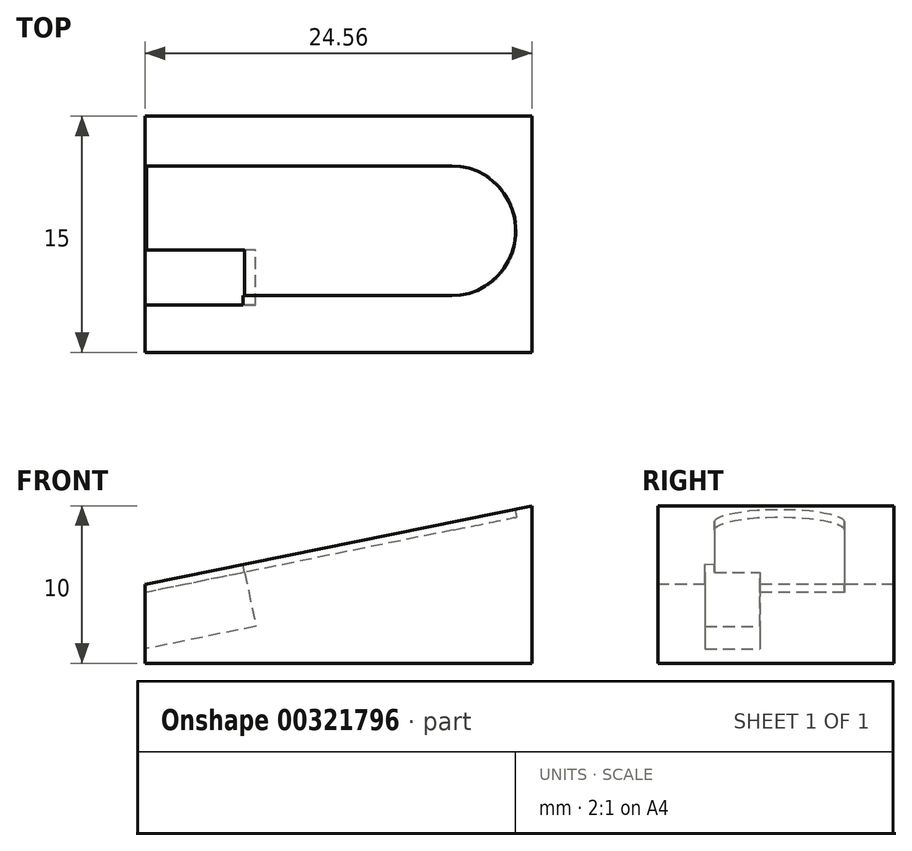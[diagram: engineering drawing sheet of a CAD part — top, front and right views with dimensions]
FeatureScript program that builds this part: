
annotation { "Feature Type Name" : "Feature", "Feature Type Description" : "" }
export const myFeature = defineFeature(function(context is Context, id is Id, definition is map)
    precondition{}
    {
        {
            var Q0;
            Q0=qCreatedBy(makeId("Front.planeOp"),FACE);
            var sketch = newSketch(context, id + "F0", { "sketchPlane" : qUnion([Q0])});
            skLineSegment(sketch, "E0.bottom", {"start": v(0, 24.14) * mm, "end": v(-24.56, 24.14) * mm});
            skLineSegment(sketch, "E0.top", {"start": v(0, 14.14) * mm, "end": v(-24.56, 14.14) * mm});
            skLineSegment(sketch, "E0.left", {"start": v(0, 24.14) * mm, "end": v(0, 14.14) * mm});
            skLineSegment(sketch, "E0.right", {"start": v(-24.56, 24.14) * mm, "end": v(-24.56, 14.14) * mm});
            skSolve(sketch);
        }
        {
            var Q0;
            Q0=makeQuery(id+"F0.imprint","IMPRINT",FACE,{"disambiguationData":[TD([[makeQuery(id+"F0.imprint","IMPRINT",EDGE,{"derivedFrom":sQuery(id+"F0.wireOp",EDGE,"E0.bottom")}),1.0]])]});
            extrude(context, id + "F1", {"entities" : qUnion([Q0]), "depth" : 15 * mm});
        }
        {
            var Q0;
            Q0=makeQuery(id+"F1.opExtrude","SWEPT_FACE",FACE,{"disambiguationData":[OSD([sQuery(id+"F0.wireOp",EDGE,"E0.left")])]});
            var sketch = newSketch(context, id + "F2", { "sketchPlane" : qUnion([Q0])});
            skLineSegment(sketch, "E1.bottom", {"start": v(-15, 24.14) * mm, "end": v(0, 24.14) * mm});
            skLineSegment(sketch, "E1.top", {"start": v(-15, 14.14) * mm, "end": v(0, 14.14) * mm});
            skLineSegment(sketch, "E1.left", {"start": v(-15, 24.14) * mm, "end": v(-15, 14.14) * mm});
            skLineSegment(sketch, "E1.right", {"start": v(0, 24.14) * mm, "end": v(0, 14.14) * mm});
            skSolve(sketch);
        }
        {
            var Q0;
            Q0=makeQuery(id+"F1.opExtrude","SWEPT_FACE",FACE,{"disambiguationData":[OSD([sQuery(id+"F0.wireOp",EDGE,"E0.right")])]});
            var sketch = newSketch(context, id + "F3", { "sketchPlane" : qUnion([Q0])});
            skLineSegment(sketch, "E2.bottom", {"start": v(0, 19.14) * mm, "end": v(15, 19.14) * mm});
            skLineSegment(sketch, "E2.top", {"start": v(0, 14.14) * mm, "end": v(15, 14.14) * mm});
            skLineSegment(sketch, "E2.left", {"start": v(0, 19.14) * mm, "end": v(0, 14.14) * mm});
            skLineSegment(sketch, "E2.right", {"start": v(15, 19.14) * mm, "end": v(15, 14.14) * mm});
            skSolve(sketch);
        }
        {
            var Q1;
            Q1 = qSketchRegion(id + "F2", true);
            var Q2;
            Q2=makeQuery(id+"F3.imprint","IMPRINT",FACE,{"disambiguationData":[TD([[makeQuery(id+"F3.imprint","IMPRINT",EDGE,{"derivedFrom":sQuery(id+"F3.wireOp",EDGE,"E2.bottom")}),-1.0]])]});
            loft(context, id + "F4", {"sheetProfilesArray" : [{ "sheetProfileEntities" : qUnion([Q1]) }, { "sheetProfileEntities" : qUnion([Q2]) }]});
        }
        {
            var Q0;
            Q0=makeQuery(id+"F1.opExtrude","SWEPT_BODY",BODY,{"disambiguationData":[OSD([sQuery(id+"F0.wireOp",EDGE,"E0.bottom"),sQuery(id+"F0.wireOp",EDGE,"E0.top"),sQuery(id+"F0.wireOp",EDGE,"E0.left"),sQuery(id+"F0.wireOp",EDGE,"E0.right")])]});
            deleteBodies(context, id + "F5", {"entities" : qUnion([Q0])});
        }
        {
            var Q0;
            Q0=makeQuery(id+"F4.opLoft","SWEPT_FACE",FACE,{"disambiguationData":[OSD([sQuery(id+"F0.wireOp",EDGE,"E0.right"),sQuery(id+"F2.wireOp",EDGE,"E1.bottom"),sQuery(id+"F2.wireOp",EDGE,"E1.left"),sQuery(id+"F2.wireOp",EDGE,"E1.right"),sQuery(id+"F3.wireOp",EDGE,"E2.bottom"),sQuery(id+"F3.wireOp",EDGE,"E2.left"),sQuery(id+"F3.wireOp",EDGE,"E2.right")])]});
            var sketch = newSketch(context, id + "F6", { "sketchPlane" : qUnion([Q0])});
            skArc(sketch, "E3", {"start": v(-0.36, -11.4) * mm, "mid": v(3.76, -7.28) * mm, "end": v(-0.36, -3.15) * mm});
            skLineSegment(sketch, "E4", {"start": v(-0.36, -3.15) * mm, "end": v(-20.25, -3.15) * mm});
            skLineSegment(sketch, "E5", {"start": v(-0.36, -11.4) * mm, "end": v(-13.9, -11.4) * mm});
            skLineSegment(sketch, "E6", {"start": v(-20.25, -12) * mm, "end": v(-13.9, -12) * mm});
            skLineSegment(sketch, "E7", {"start": v(-13.9, -11.4) * mm, "end": v(-13.9, -12) * mm});
            skSolve(sketch);
        }
        {
            var Q0;
            Q0=makeQuery(id+"F6.imprint","IMPRINT",FACE,{"disambiguationData":[TD([[makeQuery(id+"F6.imprint","IMPRINT",EDGE,{"derivedFrom":sQuery(id+"F6.wireOp",EDGE,"E3")}),1.0]])]});
            extrude(context, id + "F7", {"entities" : qUnion([Q0]), "operationType" : NewBodyOperationType.REMOVE, "oppositeDirection" : true, "depth" : 0.5 * mm});
        }
        {
            var Q0;
            Q0=makeQuery(id+"F4.opLoft","SWEPT_FACE",FACE,{"disambiguationData":[OSD([sQuery(id+"F0.wireOp",EDGE,"E0.right"),sQuery(id+"F2.wireOp",EDGE,"E1.bottom"),sQuery(id+"F2.wireOp",EDGE,"E1.left"),sQuery(id+"F2.wireOp",EDGE,"E1.right"),sQuery(id+"F3.wireOp",EDGE,"E2.bottom"),sQuery(id+"F3.wireOp",EDGE,"E2.left"),sQuery(id+"F3.wireOp",EDGE,"E2.right")])]});
            var sketch = newSketch(context, id + "F8", { "sketchPlane" : qUnion([Q0])});
            skLineSegment(sketch, "E8.bottom", {"start": v(-13.9, -12) * mm, "end": v(-21.08, -12) * mm});
            skLineSegment(sketch, "E8.top", {"start": v(-13.9, -8.5) * mm, "end": v(-21.08, -8.5) * mm});
            skLineSegment(sketch, "E8.left", {"start": v(-13.9, -12) * mm, "end": v(-13.9, -8.5) * mm});
            skLineSegment(sketch, "E8.right", {"start": v(-21.08, -12) * mm, "end": v(-21.08, -8.5) * mm});
            skSolve(sketch);
        }
        {
            var Q0;
            Q0 = qSketchRegion(id + "F8", true);
            extrude(context, id + "F9", {"entities" : qUnion([Q0]), "operationType" : NewBodyOperationType.REMOVE, "oppositeDirection" : true, "depth" : 4 * mm});
        }
        {
            var Q0;
            Q0=makeQuery(id+"F9.boolean.opBoolean","COPY",FACE,{"derivedFrom":makeQuery(id+"F9.opExtrude","SWEPT_FACE",FACE,{"disambiguationData":[OSD([sQuery(id+"F8.wireOp",EDGE,"E8.left")])]})});
            var sketch = newSketch(context, id + "F10", { "sketchPlane" : qUnion([Q0])});
            skSolve(sketch);
        }
    });
